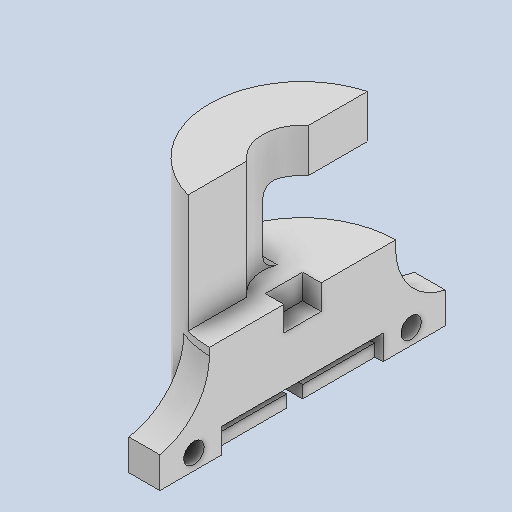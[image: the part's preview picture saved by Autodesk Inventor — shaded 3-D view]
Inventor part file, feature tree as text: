
AUTODESK INVENTOR PART (.ipt)
format: ipt  version: 2022 (Build 260153000, 153)  size: 161,792 bytes
history: native  units: in
note: dims shown in document units (in); Inventor stores cm internally (conversion verified against a paired STEP export)
features: fillet x1
ambient origin geometry x8: Origin, YZ Plane, XZ Plane, XY Plane, X Axis, Y Axis, Z Axis, Center Point
bodies: Solid1 (feature_tree)
feature tree (1):
  fillet  "Fillet2"  [1 undecoded]
note: 1 required parameter value undecoded (feature->parameter linkage not recoverable at this tier; creation-order binding heuristic only, values carry confidence <= 0.55)
